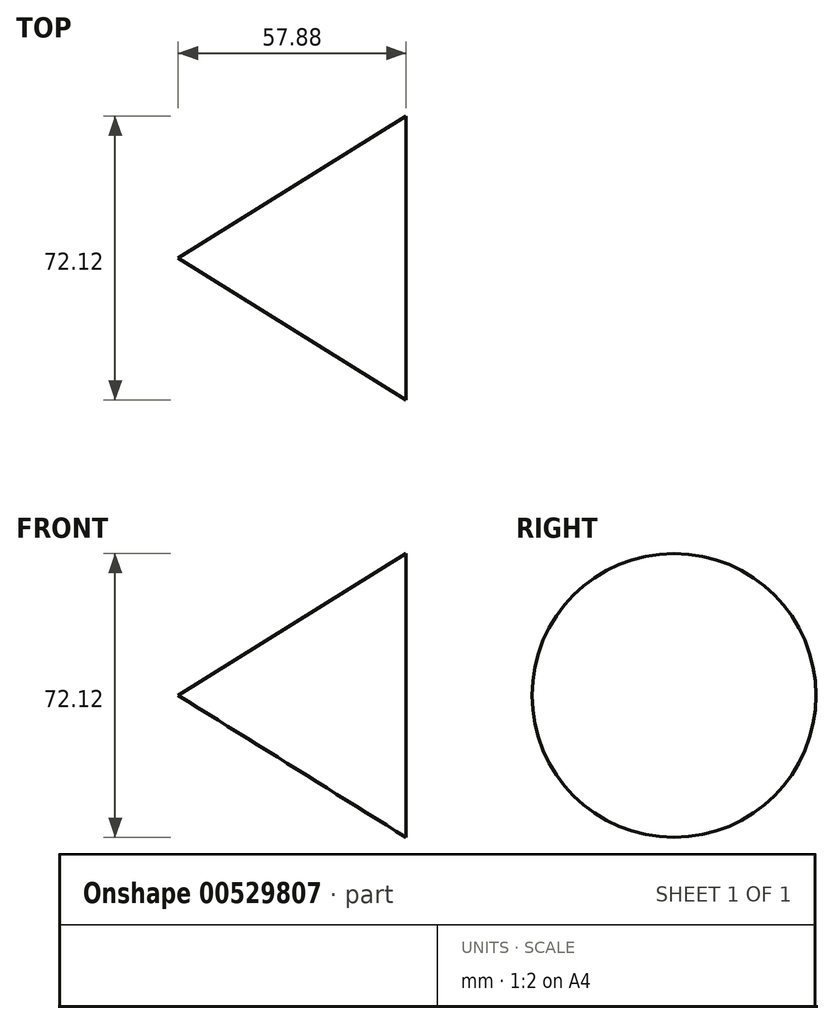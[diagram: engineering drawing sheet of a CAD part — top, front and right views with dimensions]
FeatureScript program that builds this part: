
annotation { "Feature Type Name" : "Feature", "Feature Type Description" : "" }
export const myFeature = defineFeature(function(context is Context, id is Id, definition is map)
    precondition{}
    {
        {
            var Q0;
            Q0=qCreatedBy(makeId("Top.planeOp"),FACE);
            var sketch = newSketch(context, id + "F0", { "sketchPlane" : qUnion([Q0])});
            skLineSegment(sketch, "E0", {"start": v(-29.71, 0) * mm, "end": v(28.17, 0) * mm});
            skLineSegment(sketch, "E1", {"start": v(28.17, 0) * mm, "end": v(28.17, 36.06) * mm});
            skLineSegment(sketch, "E2", {"start": v(28.17, 36.06) * mm, "end": v(-29.71, 0) * mm});
            skSolve(sketch);
        }
        {
            var Q0;
            Q0=makeQuery(id+"F0.imprint","IMPRINT",FACE,{"disambiguationData":[TD([[makeQuery(id+"F0.imprint","IMPRINT",EDGE,{"derivedFrom":sQuery(id+"F0.wireOp",EDGE,"E0")}),1.0]])]});
            var Q1;
            Q1=sQuery(id+"F0.wireOp",EDGE,"E0");
            revolve(context, id + "F1", {"entities" : qUnion([Q0]), "axis" : qUnion([Q1]), "revolveType" : RevolveType.FULL});
        }
    });
